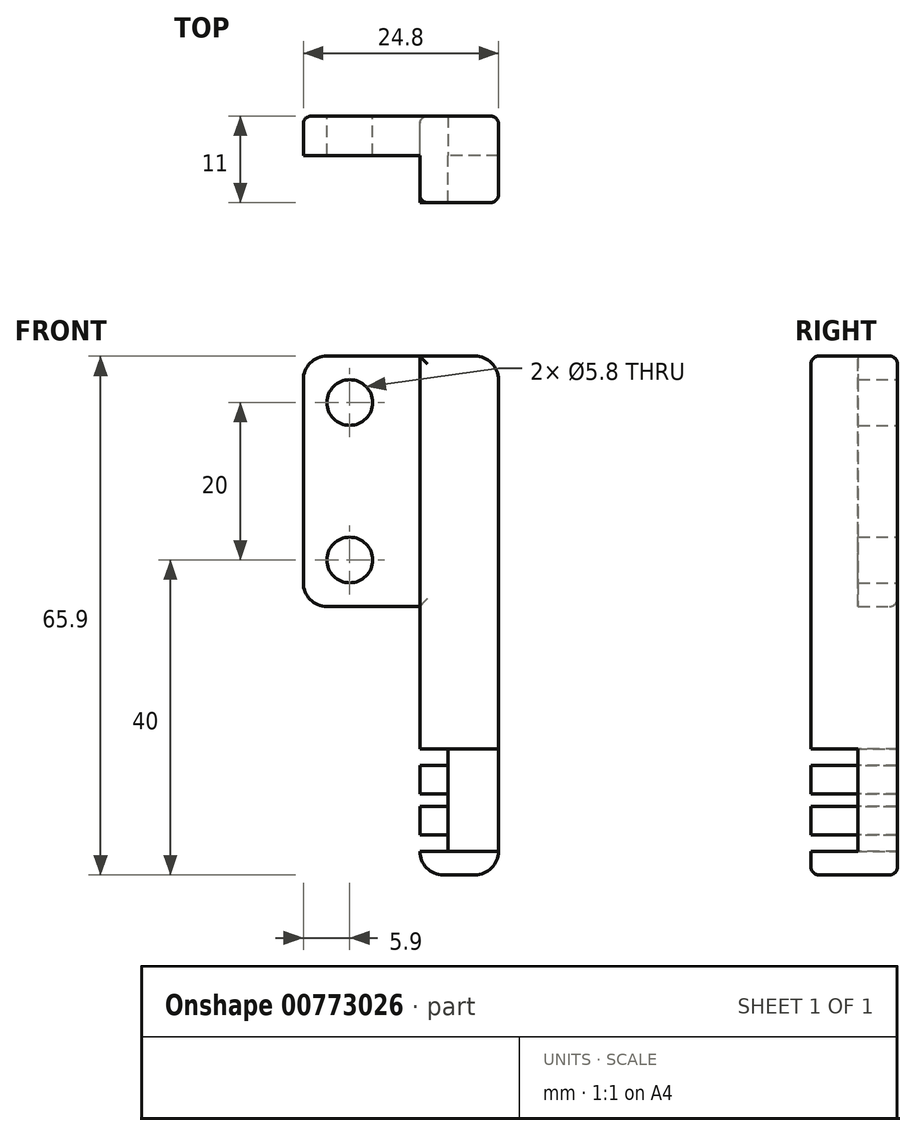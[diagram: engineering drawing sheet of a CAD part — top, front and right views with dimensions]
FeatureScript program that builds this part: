
annotation { "Feature Type Name" : "Feature", "Feature Type Description" : "" }
export const myFeature = defineFeature(function(context is Context, id is Id, definition is map)
    precondition{}
    {
        {
            var Q0;
            Q0=qCreatedBy(makeId("Front.planeOp"),FACE);
            var sketch = newSketch(context, id + "F0", { "sketchPlane" : qUnion([Q0])});
            skLineSegment(sketch, "E0.bottom", {"start": v(0, 0) * mm, "end": v(24.8, 0) * mm});
            skLineSegment(sketch, "E0.top", {"start": v(0, -31.8) * mm, "end": v(24.8, -31.8) * mm});
            skLineSegment(sketch, "E0.left", {"start": v(0, 0) * mm, "end": v(0, -31.8) * mm});
            skLineSegment(sketch, "E0.right", {"start": v(24.8, 0) * mm, "end": v(24.8, -31.8) * mm});
            skCircle(sketch, "E1", {"center": v(5.9, -5.9) * mm, "radius": 2.9 * mm});
            skCircle(sketch, "E2", {"center": v(5.9, -25.9) * mm, "radius": 2.9 * mm});
            skLineSegment(sketch, "E3", {"start": v(5.9, -5.9) * mm, "end": v(5.9, -25.9) * mm, "construction": true});
            skLineSegment(sketch, "E4.left", {"start": v(24.8, -31.8) * mm, "end": v(24.8, -65.9) * mm});
            skLineSegment(sketch, "E5.bottom", {"start": v(24.8, -65.9) * mm, "end": v(14.8, -65.9) * mm});
            skLineSegment(sketch, "E5.top", {"start": v(24.8, -31.8) * mm, "end": v(14.8, -31.8) * mm});
            skLineSegment(sketch, "E5.right", {"start": v(14.8, -65.9) * mm, "end": v(14.8, -31.8) * mm});
            skLineSegment(sketch, "E6", {"start": v(8.8, -5.9) * mm, "end": v(8.8, -31.8) * mm, "construction": true});
            skLineSegment(sketch, "E7", {"start": v(8.8, -31.8) * mm, "end": v(14.8, -31.8) * mm, "construction": true});
            skLineSegment(sketch, "E8", {"start": v(5.9, -25.9) * mm, "end": v(5.9, -65.9) * mm, "construction": true});
            skLineSegment(sketch, "E9", {"start": v(14.8, -65.9) * mm, "end": v(5.9, -65.9) * mm});
            skSolve(sketch);
        }
        {
            var Q0;
            Q0 = qSketchRegion(id + "F0", true);
            extrude(context, id + "F1", {"entities" : qUnion([Q0]), "depth" : 5 * mm, "offsetDistance" : 25 * mm});
        }
        {
            var Q0;
            Q0=makeQuery(id+"F1.opExtrude","CAP_FACE",FACE,{"disambiguationData":[OSD([sQuery(id+"F0.wireOp",EDGE,"E0.bottom"),sQuery(id+"F0.wireOp",EDGE,"E0.top"),sQuery(id+"F0.wireOp",EDGE,"E0.left"),sQuery(id+"F0.wireOp",EDGE,"E0.right"),sQuery(id+"F0.wireOp",EDGE,"E1"),sQuery(id+"F0.wireOp",EDGE,"E2"),sQuery(id+"F0.wireOp",EDGE,"E4.left"),sQuery(id+"F0.wireOp",EDGE,"E5.bottom"),sQuery(id+"F0.wireOp",EDGE,"E5.right")])],"isStart":false});
            var sketch = newSketch(context, id + "F2", { "sketchPlane" : qUnion([Q0])});
            skLineSegment(sketch, "E10", {"start": v(24.8, -65.9) * mm, "end": v(14.8, -65.9) * mm});
            skLineSegment(sketch, "E11", {"start": v(14.8, -31.8) * mm, "end": v(14.8, 0) * mm});
            skLineSegment(sketch, "E12", {"start": v(14.8, 0) * mm, "end": v(24.8, 0) * mm});
            skLineSegment(sketch, "E13", {"start": v(24.8, 0) * mm, "end": v(24.8, -65.9) * mm});
            skLineSegment(sketch, "E14.bottom", {"start": v(24.8, -49.9) * mm, "end": v(14.8, -49.9) * mm});
            skLineSegment(sketch, "E14.top", {"start": v(24.8, -62.9) * mm, "end": v(14.8, -62.9) * mm});
            skLineSegment(sketch, "E14.left", {"start": v(24.8, -49.9) * mm, "end": v(24.8, -62.9) * mm, "construction": true});
            skLineSegment(sketch, "E15", {"start": v(14.8, -62.9) * mm, "end": v(14.8, -65.9) * mm});
            skLineSegment(sketch, "E16", {"start": v(14.8, -49.9) * mm, "end": v(14.8, -31.8) * mm});
            skSolve(sketch);
        }
        {
            var Q0;
            Q0 = qSketchRegion(id + "F2", true);
            extrude(context, id + "F3", {"entities" : qUnion([Q0]), "operationType" : NewBodyOperationType.ADD, "depth" : 6 * mm, "offsetDistance" : 25 * mm});
        }
        {
            var Q0;
            {var subQ0=sQuery(id+"F0.wireOp",EDGE,"E5.right");var subQ3=sQuery(id+"F2.wireOp",EDGE,"E14.bottom");var subQ4=sQuery(id+"F0.wireOp",EDGE,"E4.left");var subQ5=sQuery(id+"F0.wireOp",EDGE,"E0.right");Q0=makeQuery(id+"F3.boolean.opBoolean","SPLIT",FACE,{"disambiguationData":[TD([makeQuery(id+"F3.opExtrude","SWEPT_FACE",FACE,{"disambiguationData":[OSD([subQ3])]})])],"derivedFrom":makeQuery(id+"F1.opExtrude","CAP_FACE",FACE,{"disambiguationData":[OSD([sQuery(id+"F0.wireOp",EDGE,"E0.bottom"),sQuery(id+"F0.wireOp",EDGE,"E0.top"),sQuery(id+"F0.wireOp",EDGE,"E0.left"),subQ5,sQuery(id+"F0.wireOp",EDGE,"E1"),sQuery(id+"F0.wireOp",EDGE,"E2"),subQ4,sQuery(id+"F0.wireOp",EDGE,"E5.bottom"),subQ0])],"isStart":false})});}
            var sketch = newSketch(context, id + "F4", { "sketchPlane" : qUnion([Q0])});
            skLineSegment(sketch, "E17.bottom", {"start": v(14.8, -49.9) * mm, "end": v(24.8, -49.9) * mm, "construction": true});
            skLineSegment(sketch, "E17.top", {"start": v(14.8, -62.9) * mm, "end": v(24.8, -62.9) * mm, "construction": true});
            skLineSegment(sketch, "E17.left", {"start": v(14.8, -49.9) * mm, "end": v(14.8, -62.9) * mm, "construction": true});
            skLineSegment(sketch, "E17.right", {"start": v(24.8, -49.9) * mm, "end": v(24.8, -62.9) * mm, "construction": true});
            skLineSegment(sketch, "E18", {"start": v(14.8, -56.4) * mm, "end": v(18.4, -56.4) * mm, "construction": true});
            skLineSegment(sketch, "E19", {"start": v(18.4, -56.4) * mm, "end": v(18.4, -55.6) * mm});
            skLineSegment(sketch, "E20.bottom", {"start": v(18.4, -55.6) * mm, "end": v(14.8, -55.6) * mm});
            skLineSegment(sketch, "E20.top", {"start": v(18.4, -52) * mm, "end": v(14.8, -52) * mm});
            skLineSegment(sketch, "E20.left", {"start": v(18.4, -55.6) * mm, "end": v(18.4, -52) * mm});
            skLineSegment(sketch, "E20.right", {"start": v(14.8, -55.6) * mm, "end": v(14.8, -52) * mm});
            skLineSegment(sketch, "E21.MirrorCS", {"start": v(18.4, -60.8) * mm, "end": v(14.8, -60.8) * mm});
            skLineSegment(sketch, "E22.MirrorCS", {"start": v(18.4, -57.2) * mm, "end": v(18.4, -60.8) * mm});
            skLineSegment(sketch, "E23.MirrorCS", {"start": v(18.4, -57.2) * mm, "end": v(14.8, -57.2) * mm});
            skLineSegment(sketch, "E24.MirrorCS", {"start": v(14.8, -57.2) * mm, "end": v(14.8, -60.8) * mm});
            skSolve(sketch);
        }
        {
            var Q0;
            Q0 = qSketchRegion(id + "F4", true);
            var Q1;
            Q1=makeQuery(id+"F3.opExtrude","CAP_FACE",FACE,{"disambiguationData":[OSD([sQuery(id+"F2.wireOp",EDGE,"E11"),sQuery(id+"F2.wireOp",EDGE,"E12"),sQuery(id+"F2.wireOp",EDGE,"E13"),sQuery(id+"F2.wireOp",EDGE,"E14.bottom"),sQuery(id+"F2.wireOp",EDGE,"E16")])],"isStart":false});
            extrude(context, id + "F5", {"entities" : qUnion([Q0]), "operationType" : NewBodyOperationType.ADD, "endBound" : BoundingType.UP_TO_SURFACE, "depth" : 25 * mm, "endBoundEntityFace" : qUnion([Q1]), "offsetDistance" : 25 * mm});
        }
        {
            var Q0;
            {var subQ0=sQuery(id+"F0.wireOp",EDGE,"E5.right");var subQ3=sQuery(id+"F2.wireOp",EDGE,"E14.bottom");var subQ4=sQuery(id+"F0.wireOp",EDGE,"E4.left");var subQ5=sQuery(id+"F0.wireOp",EDGE,"E0.right");Q0=makeQuery(id+"F3.boolean.opBoolean","SPLIT",FACE,{"disambiguationData":[TD([makeQuery(id+"F3.opExtrude","SWEPT_FACE",FACE,{"disambiguationData":[OSD([subQ3])]})])],"derivedFrom":makeQuery(id+"F1.opExtrude","CAP_FACE",FACE,{"disambiguationData":[OSD([sQuery(id+"F0.wireOp",EDGE,"E0.bottom"),sQuery(id+"F0.wireOp",EDGE,"E0.top"),sQuery(id+"F0.wireOp",EDGE,"E0.left"),subQ5,sQuery(id+"F0.wireOp",EDGE,"E1"),sQuery(id+"F0.wireOp",EDGE,"E2"),subQ4,sQuery(id+"F0.wireOp",EDGE,"E5.bottom"),subQ0])],"isStart":false})});}
            var sketch = newSketch(context, id + "F6", { "sketchPlane" : qUnion([Q0])});
            skLineSegment(sketch, "E25.bottom", {"start": v(14.8, -49.9) * mm, "end": v(18.4, -49.9) * mm});
            skLineSegment(sketch, "E25.top", {"start": v(14.8, -52) * mm, "end": v(18.4, -52) * mm});
            skLineSegment(sketch, "E25.left", {"start": v(14.8, -49.9) * mm, "end": v(14.8, -52) * mm});
            skLineSegment(sketch, "E25.right", {"start": v(18.4, -49.9) * mm, "end": v(18.4, -52) * mm});
            skLineSegment(sketch, "E26.bottom", {"start": v(14.8, -55.6) * mm, "end": v(18.4, -55.6) * mm});
            skLineSegment(sketch, "E26.top", {"start": v(14.8, -57.2) * mm, "end": v(18.4, -57.2) * mm});
            skLineSegment(sketch, "E26.left", {"start": v(14.8, -55.6) * mm, "end": v(14.8, -57.2) * mm});
            skLineSegment(sketch, "E26.right", {"start": v(18.4, -55.6) * mm, "end": v(18.4, -57.2) * mm});
            skLineSegment(sketch, "E27.bottom", {"start": v(14.8, -60.8) * mm, "end": v(18.4, -60.8) * mm});
            skLineSegment(sketch, "E27.top", {"start": v(14.8, -62.9) * mm, "end": v(18.4, -62.9) * mm});
            skLineSegment(sketch, "E27.left", {"start": v(14.8, -60.8) * mm, "end": v(14.8, -62.9) * mm});
            skLineSegment(sketch, "E27.right", {"start": v(18.4, -60.8) * mm, "end": v(18.4, -62.9) * mm});
            skSolve(sketch);
        }
        {
            var Q0;
            Q0 = qSketchRegion(id + "F6", true);
            extrude(context, id + "F7", {"entities" : qUnion([Q0]), "operationType" : NewBodyOperationType.REMOVE, "endBound" : BoundingType.THROUGH_ALL, "oppositeDirection" : true, "depth" : 25 * mm, "offsetDistance" : 25 * mm});
        }
        {
            var Q0;
            Q0=makeQuery(id+"F1.opExtrude","SWEPT_EDGE",EDGE,{"disambiguationData":[OSD([sQuery(id+"F0.wireOp",EDGE,"E0.top"),sQuery(id+"F0.wireOp",EDGE,"E0.left")])]});
            var Q1;
            Q1=makeQuery(id+"F1.opExtrude","SWEPT_EDGE",EDGE,{"disambiguationData":[OSD([sQuery(id+"F0.wireOp",EDGE,"E0.bottom"),sQuery(id+"F0.wireOp",EDGE,"E0.left")])]});
            var Q2;
            Q2=makeQuery(id+"F3.boolean.opBoolean","MERGE",EDGE,{"derivedFrom":[makeQuery(id+"F1.opExtrude","SWEPT_EDGE",EDGE,{"disambiguationData":[OSD([sQuery(id+"F0.wireOp",EDGE,"E0.bottom"),sQuery(id+"F0.wireOp",EDGE,"E0.right")])]}),makeQuery(id+"F3.opExtrude","SWEPT_EDGE",EDGE,{"disambiguationData":[OSD([sQuery(id+"F2.wireOp",EDGE,"E12"),sQuery(id+"F2.wireOp",EDGE,"E13")])]})]});
            var Q3;
            Q3=makeQuery(id+"F3.boolean.opBoolean","MERGE",EDGE,{"derivedFrom":[makeQuery(id+"F1.opExtrude","SWEPT_EDGE",EDGE,{"disambiguationData":[OSD([sQuery(id+"F0.wireOp",EDGE,"E4.left"),sQuery(id+"F0.wireOp",EDGE,"E5.bottom")])]}),makeQuery(id+"F3.opExtrude","SWEPT_EDGE",EDGE,{"disambiguationData":[OSD([sQuery(id+"F2.wireOp",EDGE,"E10"),sQuery(id+"F2.wireOp",EDGE,"E13")])]})]});
            var Q4;
            Q4=makeQuery(id+"F3.boolean.opBoolean","MERGE",EDGE,{"derivedFrom":[makeQuery(id+"F1.opExtrude","SWEPT_EDGE",EDGE,{"disambiguationData":[OSD([sQuery(id+"F0.wireOp",EDGE,"E5.bottom"),sQuery(id+"F0.wireOp",EDGE,"E5.right")])]}),makeQuery(id+"F3.opExtrude","SWEPT_EDGE",EDGE,{"disambiguationData":[OSD([sQuery(id+"F2.wireOp",EDGE,"E10"),sQuery(id+"F2.wireOp",EDGE,"E15")])]})]});
            fillet(context, id + "F8", {"entities" : qUnion([Q0, Q1, Q2, Q3, Q4]), "radius" : 3 * mm, "tangentPropagation" : true, "allowEdgeOverflow" : false});
        }
        {
            var Q0;
            {var subQ0=sQuery(id+"F0.wireOp",EDGE,"E5.right");Q0=makeQuery(id+"F7.boolean.opBoolean","SPLIT",EDGE,{"disambiguationData":[TD([makeQuery(id+"F5.opExtrude","SWEPT_FACE",FACE,{"disambiguationData":[OSD([sQuery(id+"F4.wireOp",EDGE,"E20.bottom")])]})])],"derivedFrom":makeQuery(id+"F1.opExtrude","CAP_EDGE",EDGE,{"disambiguationData":[OSD([subQ0])],"isStart":true})});}
            var Q1;
            {var subQ0=sQuery(id+"F0.wireOp",EDGE,"E5.right");Q1=makeQuery(id+"F7.boolean.opBoolean","SPLIT",EDGE,{"disambiguationData":[TD([makeQuery(id+"F5.opExtrude","SWEPT_FACE",FACE,{"disambiguationData":[OSD([sQuery(id+"F4.wireOp",EDGE,"E21.MirrorCS")])]})])],"derivedFrom":makeQuery(id+"F1.opExtrude","CAP_EDGE",EDGE,{"disambiguationData":[OSD([subQ0])],"isStart":true})});}
            var Q2;
            {var subQ0=sQuery(id+"F0.wireOp",EDGE,"E5.right");var subQ1=sQuery(id+"F0.wireOp",EDGE,"E0.top");Q2=makeQuery(id+"F7.boolean.opBoolean","SPLIT",EDGE,{"disambiguationData":[TD([makeQuery(id+"F1.opExtrude","SWEPT_FACE",FACE,{"disambiguationData":[OSD([subQ1])]})])],"derivedFrom":makeQuery(id+"F1.opExtrude","CAP_EDGE",EDGE,{"disambiguationData":[OSD([subQ0])],"isStart":true})});}
            var Q3;
            {var subQ0=sQuery(id+"F2.wireOp",EDGE,"E13");Q3=makeQuery(id+"F3.opExtrude","CAP_EDGE",EDGE,{"disambiguationData":[OSD([subQ0]),TDD([makeQuery(id+"F2.imprint","IMPRINT",EDGE,{"disambiguationData":[TD([[makeQuery(id+"F2.imprint","INTERSECT",VERTEX,{"derivedFrom":[sQuery(id+"F2.wireOp",EDGE,"E12"),subQ0]}),-1.0]])],"derivedFrom":subQ0})])],"isStart":false});}
            var Q4;
            {var subQ0=sQuery(id+"F0.wireOp",EDGE,"E5.right");var subQ1=sQuery(id+"F0.wireOp",EDGE,"E5.bottom");Q4=makeQuery(id+"F8.opFillet","BLEND_EDGE",EDGE,{"blendedFrom":[makeQuery(id+"F3.boolean.opBoolean","MERGE",EDGE,{"derivedFrom":[makeQuery(id+"F1.opExtrude","SWEPT_EDGE",EDGE,{"disambiguationData":[OSD([subQ1,subQ0])]}),makeQuery(id+"F3.opExtrude","SWEPT_EDGE",EDGE,{"disambiguationData":[OSD([sQuery(id+"F2.wireOp",EDGE,"E10"),sQuery(id+"F2.wireOp",EDGE,"E15")])]})]}),makeQuery(id+"F1.opExtrude","CAP_FACE",FACE,{"disambiguationData":[OSD([sQuery(id+"F0.wireOp",EDGE,"E0.bottom"),sQuery(id+"F0.wireOp",EDGE,"E0.top"),sQuery(id+"F0.wireOp",EDGE,"E0.left"),sQuery(id+"F0.wireOp",EDGE,"E0.right"),sQuery(id+"F0.wireOp",EDGE,"E1"),sQuery(id+"F0.wireOp",EDGE,"E2"),sQuery(id+"F0.wireOp",EDGE,"E4.left"),subQ1,subQ0])],"isStart":true})],"blendedInto":[makeQuery(id+"F1.opExtrude","CAP_FACE",FACE,{"disambiguationData":[OSD([sQuery(id+"F0.wireOp",EDGE,"E0.bottom"),sQuery(id+"F0.wireOp",EDGE,"E0.top"),sQuery(id+"F0.wireOp",EDGE,"E0.left"),sQuery(id+"F0.wireOp",EDGE,"E0.right"),sQuery(id+"F0.wireOp",EDGE,"E1"),sQuery(id+"F0.wireOp",EDGE,"E2"),sQuery(id+"F0.wireOp",EDGE,"E4.left"),subQ1,subQ0])],"isStart":true})]});}
            var Q5;
            Q5=makeQuery(id+"F3.opExtrude","CAP_EDGE",EDGE,{"disambiguationData":[OSD([sQuery(id+"F2.wireOp",EDGE,"E11"),sQuery(id+"F2.wireOp",EDGE,"E16")])],"isStart":false});
            var Q6;
            {var subQ0=sQuery(id+"F2.wireOp",EDGE,"E13");var subQ1=sQuery(id+"F2.wireOp",EDGE,"E10");Q6=makeQuery(id+"F8.opFillet","BLEND_EDGE",EDGE,{"blendedFrom":[makeQuery(id+"F3.boolean.opBoolean","MERGE",EDGE,{"derivedFrom":[makeQuery(id+"F1.opExtrude","SWEPT_EDGE",EDGE,{"disambiguationData":[OSD([sQuery(id+"F0.wireOp",EDGE,"E4.left"),sQuery(id+"F0.wireOp",EDGE,"E5.bottom")])]}),makeQuery(id+"F3.opExtrude","SWEPT_EDGE",EDGE,{"disambiguationData":[OSD([subQ1,subQ0])]})]}),makeQuery(id+"F3.opExtrude","CAP_FACE",FACE,{"disambiguationData":[OSD([subQ1,subQ0,sQuery(id+"F2.wireOp",EDGE,"E14.top"),sQuery(id+"F2.wireOp",EDGE,"E15")])],"isStart":false})],"blendedInto":[makeQuery(id+"F3.opExtrude","CAP_FACE",FACE,{"disambiguationData":[OSD([subQ1,subQ0,sQuery(id+"F2.wireOp",EDGE,"E14.top"),sQuery(id+"F2.wireOp",EDGE,"E15")])],"isStart":false})]});}
            var Q7;
            Q7=makeQuery(id+"F5.opExtrude","TWEAK_EDGE",EDGE,{"derivedFrom":[makeQuery(id+"F3.opExtrude","CAP_FACE",FACE,{"disambiguationData":[OSD([sQuery(id+"F2.wireOp",EDGE,"E11"),sQuery(id+"F2.wireOp",EDGE,"E12"),sQuery(id+"F2.wireOp",EDGE,"E13"),sQuery(id+"F2.wireOp",EDGE,"E14.bottom"),sQuery(id+"F2.wireOp",EDGE,"E16")])],"isStart":false}),makeQuery(id+"F4.imprint","IMPRINT",EDGE,{"derivedFrom":sQuery(id+"F4.wireOp",EDGE,"E20.right")})]});
            var Q8;
            Q8=makeQuery(id+"F5.opExtrude","TWEAK_EDGE",EDGE,{"derivedFrom":[makeQuery(id+"F3.opExtrude","CAP_FACE",FACE,{"disambiguationData":[OSD([sQuery(id+"F2.wireOp",EDGE,"E11"),sQuery(id+"F2.wireOp",EDGE,"E12"),sQuery(id+"F2.wireOp",EDGE,"E13"),sQuery(id+"F2.wireOp",EDGE,"E14.bottom"),sQuery(id+"F2.wireOp",EDGE,"E16")])],"isStart":false}),makeQuery(id+"F4.imprint","IMPRINT",EDGE,{"derivedFrom":sQuery(id+"F4.wireOp",EDGE,"E24.MirrorCS")})]});
            fillet(context, id + "F9", {"entities" : qUnion([Q0, Q1, Q2, Q3, Q4, Q5, Q6, Q7, Q8]), "radius" : 1 * mm, "tangentPropagation" : true, "allowEdgeOverflow" : false});
        }
    });
